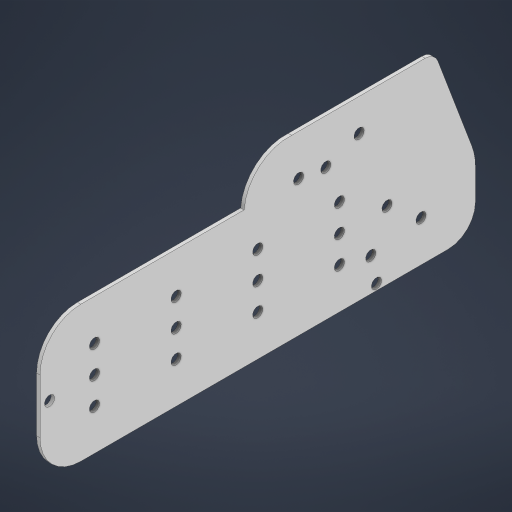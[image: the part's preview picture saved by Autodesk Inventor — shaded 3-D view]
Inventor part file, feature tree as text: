
AUTODESK INVENTOR PART (.ipt)
format: ipt  version: 2024 (Build 280153000, 153)  size: 257,536 bytes
history: native  units: in
note: dims shown in document units (in); Inventor stores cm internally (conversion verified against a paired STEP export)
features: sketch x1, extrude x1, hole x1
ambient origin geometry x8: Origin, YZ Plane, XZ Plane, XY Plane, X Axis, Y Axis, Z Axis, Center Point
bodies: Solid1 (feature_tree)
feature tree (3):
  sketch  "Sketch1"  dims[d0=8.0in d1=2.5in d4=0.0625in d5=0.0in d13=1.5in d14=1.5in d15=1.5in d17=0.5in d18=0.5in d19=0.875in d20=0.1875in d21=0.75in d22=0.375in d23=0.25in d24=0.5635in d25=1.0in d26=0.8108in d28=0.75in d29=0.75in d31=1.5in d32=0.1374in d33=1.5in d34=1.5in d35=1.5in d36=1.5in d40=0.5in d41=1.0994in d42=0.5in d43=0.5in d44=0.07in d45=0.75in d46=0.75in d48=0.5in d49=0.07in d50=3.0in d51=0.75in d52=0.75in d53=0.875in d54=2.0in d55=0.5in d56=0.25in d57=1.0in d58=0.825in]
  extrude  "Extrusion1"  Depth=2.5in
  hole  "Hole2"  [1 undecoded]
note: 1 required parameter value undecoded (feature->parameter linkage not recoverable at this tier; creation-order binding heuristic only, values carry confidence <= 0.55)
